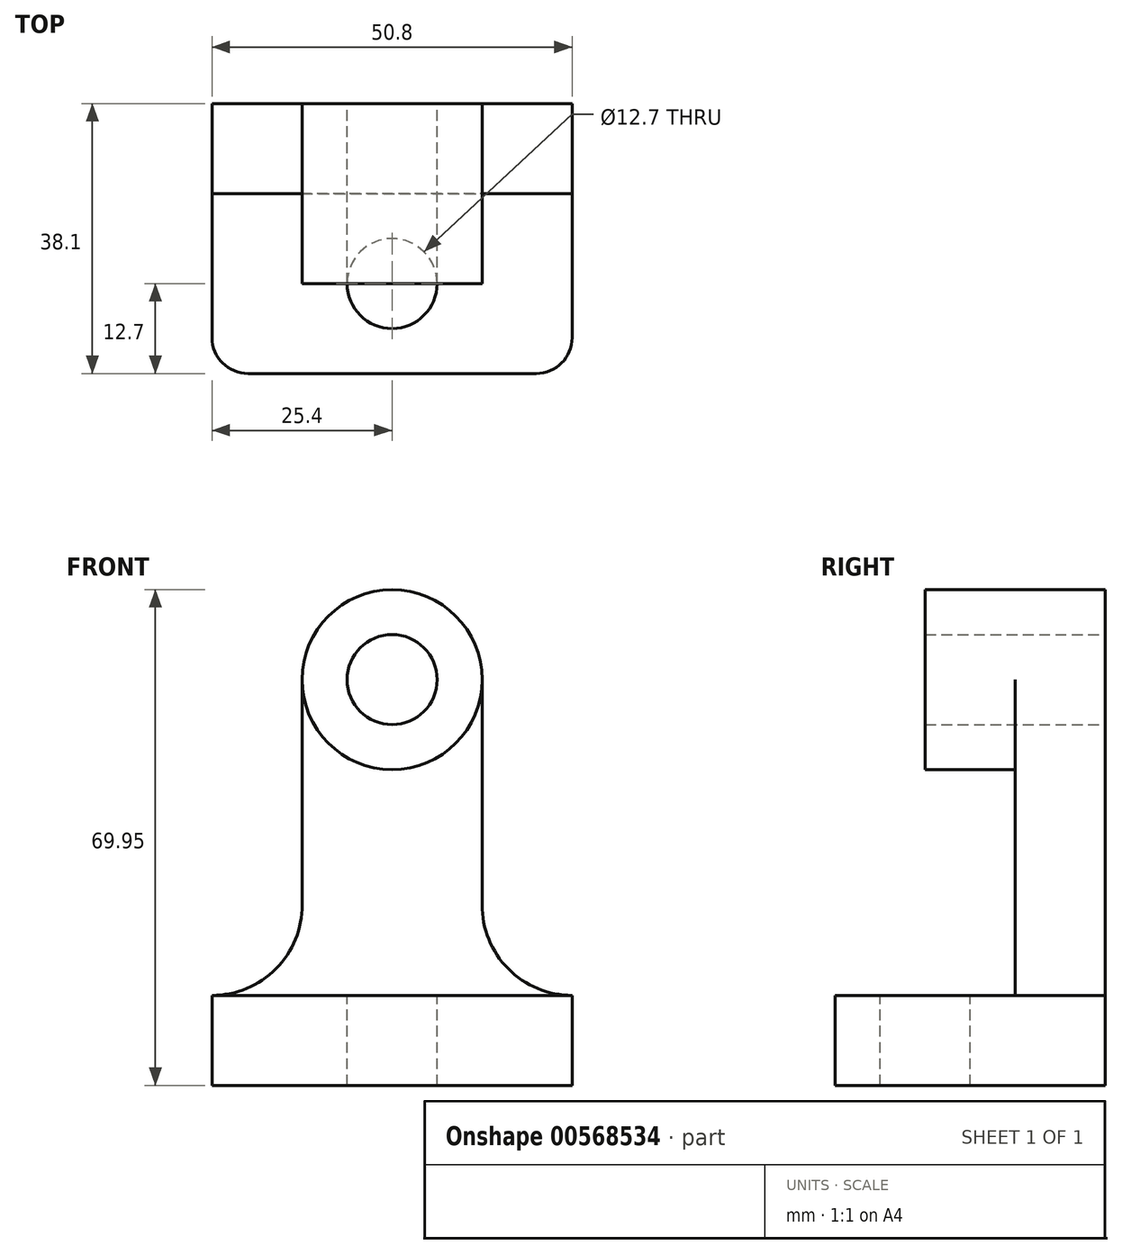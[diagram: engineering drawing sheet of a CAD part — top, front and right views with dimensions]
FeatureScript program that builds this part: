
annotation { "Feature Type Name" : "Feature", "Feature Type Description" : "" }
export const myFeature = defineFeature(function(context is Context, id is Id, definition is map)
    precondition{}
    {
        {
            var Q0;
            Q0=qCreatedBy(makeId("Front.planeOp"),FACE);
            var sketch = newSketch(context, id + "F0", { "sketchPlane" : qUnion([Q0])});
            skLineSegment(sketch, "E0", {"start": v(-38.1, 0) * mm, "end": v(12.7, 0) * mm});
            skLineSegment(sketch, "E1", {"start": v(12.7, 0) * mm, "end": v(12.7, 12.7) * mm});
            skLineSegment(sketch, "E2", {"start": v(12.7, 12.7) * mm, "end": v(-38.1, 12.7) * mm});
            skLineSegment(sketch, "E3", {"start": v(-38.1, 12.7) * mm, "end": v(-38.1, 0) * mm});
            skLineSegment(sketch, "E4", {"start": v(-25.4, 25.5) * mm, "end": v(-25.4, 57.25) * mm});
            skLineSegment(sketch, "E5", {"start": v(0, 25.5) * mm, "end": v(0, 57.25) * mm});
            skPoint(sketch, "E6.centerSnap0", {"position": v(-12.7, 12.7) * mm});
            skLineSegment(sketch, "E7", {"start": v(-25.4, 57.25) * mm, "end": v(0, 57.25) * mm});
            skCircle(sketch, "E8", {"center": v(-12.7, 57.25) * mm, "radius": 12.7 * mm});
            skCircle(sketch, "E9", {"center": v(-12.7, 57.25) * mm, "radius": 6.35 * mm});
            skArc(sketch, "E10", {"start": v(0, 25.5) * mm, "mid": v(3.68, 16.46) * mm, "end": v(12.7, 12.7) * mm});
            skArc(sketch, "E11", {"start": v(-38.1, 12.7) * mm, "mid": v(-29.08, 16.46) * mm, "end": v(-25.4, 25.5) * mm});
            skSolve(sketch);
        }
        {
            var Q0;
            {var subQ1=sQuery(id+"F0.wireOp",EDGE,"E7");var subQ3=sQuery(id+"F0.wireOp",EDGE,"E9");var subQ4=makeQuery(id+"F0.imprint","INTERSECT",VERTEX,{"disambiguationData":[OD(0.0)],"derivedFrom":[subQ1,subQ3]});Q0=makeQuery(id+"F0.imprint","IMPRINT",FACE,{"disambiguationData":[TD([[makeQuery(id+"F0.imprint","IMPRINT",EDGE,{"disambiguationData":[TD([[subQ4,-1.0]])],"derivedFrom":subQ3}),-1.0]])]});}
            var Q1;
            {var subQ1=sQuery(id+"F0.wireOp",EDGE,"E7");var subQ3=sQuery(id+"F0.wireOp",EDGE,"E9");var subQ4=makeQuery(id+"F0.imprint","INTERSECT",VERTEX,{"disambiguationData":[OD(0.0)],"derivedFrom":[subQ1,subQ3]});Q1=makeQuery(id+"F0.imprint","IMPRINT",FACE,{"disambiguationData":[TD([[makeQuery(id+"F0.imprint","IMPRINT",EDGE,{"disambiguationData":[TD([[subQ4,1.0]])],"derivedFrom":subQ3}),-1.0]])]});}
            extrude(context, id + "F1", {"entities" : qUnion([Q0, Q1]), "depth" : 25.4 * mm, "offsetDistance" : 25.4 * mm});
        }
        {
            var Q0;
            {var subQ2=sQuery(id+"F0.wireOp",EDGE,"E4");Q0=makeQuery(id+"F0.imprint","IMPRINT",FACE,{"disambiguationData":[TD([[makeQuery(id+"F0.imprint","IMPRINT",EDGE,{"derivedFrom":subQ2}),-1.0]])]});}
            extrude(context, id + "F2", {"entities" : qUnion([Q0]), "operationType" : NewBodyOperationType.ADD, "depth" : 12.7 * mm, "offsetDistance" : 25.4 * mm});
        }
        {
            var Q0;
            Q0=makeQuery(id+"F0.imprint","IMPRINT",FACE,{"disambiguationData":[TD([[makeQuery(id+"F0.imprint","IMPRINT",EDGE,{"derivedFrom":sQuery(id+"F0.wireOp",EDGE,"E0")}),1.0]])]});
            extrude(context, id + "F3", {"entities" : qUnion([Q0]), "operationType" : NewBodyOperationType.ADD, "depth" : 38.1 * mm, "offsetDistance" : 25.4 * mm});
        }
        {
            var Q0;
            Q0=makeQuery(id+"F3.opExtrude","SWEPT_FACE",FACE,{"disambiguationData":[OSD([sQuery(id+"F0.wireOp",EDGE,"E2")])]});
            var sketch = newSketch(context, id + "F4", { "sketchPlane" : qUnion([Q0])});
            skCircle(sketch, "E12", {"center": v(-12.7, -25.4) * mm, "radius": 6.35 * mm});
            skPoint(sketch, "E12.centerSnap0", {"position": v(-12.7, -38.1) * mm});
            skPoint(sketch, "E12.centerSnap1", {"position": v(-38.1, -25.4) * mm});
            skSolve(sketch);
        }
        {
            var Q0;
            Q0 = qSketchRegion(id + "F4", true);
            extrude(context, id + "F5", {"entities" : qUnion([Q0]), "operationType" : NewBodyOperationType.REMOVE, "endBound" : BoundingType.THROUGH_ALL, "oppositeDirection" : true, "depth" : 25.4 * mm, "offsetDistance" : 25.4 * mm});
        }
        {
            var Q0;
            Q0=makeQuery(id+"F3.opExtrude","CAP_EDGE",EDGE,{"disambiguationData":[OSD([sQuery(id+"F0.wireOp",EDGE,"E1")])],"isStart":false});
            var Q1;
            Q1=makeQuery(id+"F3.opExtrude","CAP_EDGE",EDGE,{"disambiguationData":[OSD([sQuery(id+"F0.wireOp",EDGE,"E3")])],"isStart":false});
            fillet(context, id + "F6", {"entities" : qUnion([Q0, Q1]), "radius" : 5.08 * mm, "tangentPropagation" : true, "allowEdgeOverflow" : false});
        }
    });
